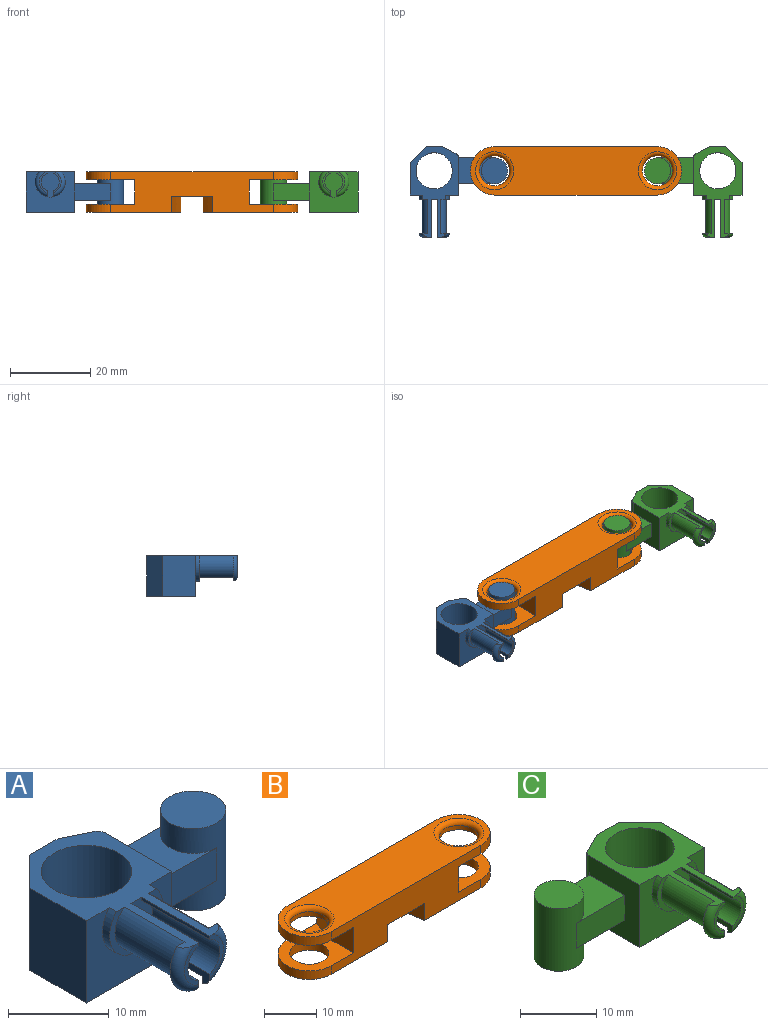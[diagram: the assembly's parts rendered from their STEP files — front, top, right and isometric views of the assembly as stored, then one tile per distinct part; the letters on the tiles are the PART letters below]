
ASSEMBLY  parts=3 mates=2
PART A: 33 faces, bbox 24.4x22.6x11.3 mm
  f0: plane 6.17x3mm, normal (0,1,0), area 5.5mm2, adj f3,f4,f27,f31
  f1: plane 9.5x0.38mm, normal (-1,0,0), area 3.6mm2, adj f2,f4,f5,f6
  f2: cylinder r=2.25mm len=9.5mm, axis (0,1,0), area 52.6mm2, adj f1,f3,f5,f6
  f3: plane 9.64x1.69mm, normal (-1,0,0), area 8mm2, adj f0,f2,f5,f6,f27,f31
  f4: plane 22.5x12mm, normal (0,0,1), area 92.8mm2, adj f0,f1,f5,f6,f7,f8,f10,f11
  f5: plane 5.15x2mm, normal (0,-1,0), area 3.1mm2, adj f1,f2,f3,f4,f31
  f6: plane 7.5x6.25mm, normal (0,-1,0), area 29.7mm2, adj f1,f2,f3,f4,f18,f21,f24,f25
  f7: plane 10x8mm, normal (-1,0,0), area 80mm2, adj f4,f9,f10,f19
  f8: plane 10x9.38mm, normal (1,0,0), area 67.8mm2, adj f4,f9,f14,f15,f16,f17,f19,f20
  f9: plane 12x12mm, normal (0,0,-1), area 68.3mm2, adj f7,f8,f10,f11,f12,f13,f19,f20
  f10: plane 10x4mm, normal (-0.71,0.71,0), area 56.6mm2, adj f4,f7,f9,f13
  f11: plane 10x3.45mm, normal (0.45,0.89,0), area 38.5mm2, adj f4,f9,f13,f20
  f12: cylinder r=4.5mm len=10mm, axis (0,0,-1), area 282.7mm2, adj f4,f9
  f13: plane 10x4mm, normal (0,1,0), area 40mm2, adj f4,f9,f10,f11
  f14: plane 9x4mm, normal (0,1,0), area 36mm2, adj f8,f16,f17,f28
  f15: plane 9x4mm, normal (0,-1,0), area 36mm2, adj f8,f16,f17,f28
  f16: plane 9x6.5mm, normal (0,0,1), area 41.9mm2, adj f8,f14,f15,f28
  f17: plane 9x6.5mm, normal (0,0,-1), area 41.9mm2, adj f8,f14,f15,f28
  f18: cylinder r=3.75mm len=7.5mm, axis (0,-1,0), area 17.3mm2, adj f4,f6,f19
  f19: plane 12x10mm, normal (0,-1,0), area 80.7mm2, adj f4,f7,f8,f9,f18
  f20: cylinder r=1mm len=10mm, axis (0,0,-1), area 11.1mm2, adj f4,f8,f9,f11
  f21: plane 9.64x1.69mm, normal (1,0,0), area 8mm2, adj f6,f22,f23,f24,f26,f32
  f22: plane 5.15x2mm, normal (0,-1,0), area 3.1mm2, adj f4,f21,f24,f25,f32
  f23: plane 6.17x3mm, normal (0,1,0), area 5.5mm2, adj f4,f21,f26,f32
  f24: cylinder r=2.25mm len=9.5mm, axis (0,1,0), area 52.6mm2, adj f6,f21,f22,f25
  f25: plane 9.5x0.38mm, normal (1,0,0), area 3.6mm2, adj f4,f6,f22,f24
  f26: cylinder r=3mm len=8.5mm, axis (0,1,0), area 58.7mm2, adj f4,f6,f21,f23
  f27: cylinder r=3mm len=8.5mm, axis (0,1,0), area 58.7mm2, adj f0,f3,f4,f6
  f28: cylinder r=3.25mm len=10mm, axis (0,0,-1), area 163.4mm2, adj f14,f15,f16,f17,f29,f30
  f29: plane 6.5x6.5mm, normal (0,0,1), area 33.2mm2, adj f28
  f30: plane 6.5x6.5mm, normal (0,0,-1), area 33.2mm2, adj f28
  f31: torus R=2.75mm, axis (0,-1,0), area 11.6mm2, adj f0,f3,f4,f5
  f32: torus R=2.75mm, axis (0,-1,0), area 11.6mm2, adj f4,f21,f22,f23
PART B: 26 faces, bbox 52.5x12.4x10 mm
  f0: plane 40.5x10mm, normal (0,1,0), area 286.5mm2, adj f1,f2,f5,f6,f7,f11,f12,f13
  f1: plane 23.83x12.39mm, normal (0,0,-1), area 207.6mm2, adj f0,f7,f8,f9,f21
  f2: cylinder r=6mm len=12mm, axis (0,0,-1), area 37.7mm2, adj f0,f8,f11,f16
  f3: cylinder r=3.75mm len=7.5mm, axis (0,0,-1), area 23.6mm2, adj f16,f25
  f4: cylinder r=3.75mm len=7.5mm, axis (0,0,-1), area 23.6mm2, adj f13,f24
  f5: cylinder r=6mm len=12mm, axis (0,0,-1), area 37.7mm2, adj f0,f8,f11,f13
  f6: cylinder r=6mm len=12mm, axis (0,0,-1), area 37.7mm2, adj f0,f8,f12,f14
  f7: cylinder r=6mm len=12mm, axis (0,0,-1), area 37.7mm2, adj f0,f1,f8,f17
  f8: plane 40.5x10mm, normal (0,-1,0), area 293mm2, adj f1,f2,f5,f6,f7,f11,f12,f13
  f9: cylinder r=3.75mm len=7.5mm, axis (0,0,-1), area 47.1mm2, adj f1,f17
  f10: cylinder r=3.75mm len=7.5mm, axis (0,0,-1), area 47.1mm2, adj f12,f14
  f11: plane 52.5x12mm, normal (0,0,1), area 457.3mm2, adj f0,f2,f5,f8,f24,f25
  f12: plane 23.83x12.39mm, normal (0,0,-1), area 207.6mm2, adj f0,f6,f8,f10,f22
  f13: plane 14x12mm, normal (0,0,-1), area 89.4mm2, adj f0,f4,f5,f8,f15,f19
  f14: plane 14x12mm, normal (0,0,1), area 89.4mm2, adj f0,f6,f8,f10,f15,f19
  f15: plane 7x6mm, normal (1,0,0), area 42mm2, adj f8,f13,f14,f19
  f16: plane 14x12mm, normal (0,0,-1), area 89.4mm2, adj f0,f2,f3,f8,f18,f20
  f17: plane 14x12mm, normal (0,0,1), area 89.4mm2, adj f0,f7,f8,f9,f18,f20
  f18: plane 7x6mm, normal (-1,0,0), area 42mm2, adj f8,f16,f17,f20
  f19: plane 6x5mm, normal (0.93,0.37,0), area 32.3mm2, adj f0,f13,f14,f15
  f20: plane 6x5mm, normal (-0.93,0.37,0), area 32.3mm2, adj f0,f16,f17,f18
  f21: extruded ~12x4mm, area 48.8mm2, adj f0,f1,f8,f23
  f22: extruded ~12x4mm, area 48.8mm2, adj f0,f8,f12,f23
  f23: plane 12.39x10mm, normal (0,0,-1), area 95.6mm2, adj f0,f8,f21,f22
  f24: torus R=4.75mm, axis (0,0,1), area 40.6mm2, adj f4,f11
  f25: torus R=4.75mm, axis (0,0,1), area 40.6mm2, adj f3,f11
PART C: 33 faces, bbox 24.4x22.6x11.3 mm
  f0: plane 6.17x3mm, normal (0,1,0), area 5.5mm2, adj f3,f4,f27,f31
  f1: plane 9.5x0.38mm, normal (1,0,0), area 3.6mm2, adj f2,f4,f5,f6
  f2: cylinder r=2.25mm len=9.5mm, axis (0,1,0), area 52.6mm2, adj f1,f3,f5,f6
  f3: plane 9.64x1.69mm, normal (1,0,0), area 8mm2, adj f0,f2,f5,f6,f27,f31
  f4: plane 22.5x12mm, normal (0,0,1), area 92.8mm2, adj f0,f1,f5,f6,f7,f8,f10,f11
  f5: plane 5.15x2mm, normal (0,-1,0), area 3.1mm2, adj f1,f2,f3,f4,f31
  f6: plane 7.5x6.25mm, normal (0,-1,0), area 29.7mm2, adj f1,f2,f3,f4,f18,f21,f24,f25
  f7: plane 10x8mm, normal (1,0,0), area 80mm2, adj f4,f9,f10,f19
  f8: plane 10x9.38mm, normal (-1,0,0), area 67.8mm2, adj f4,f9,f14,f15,f16,f17,f19,f20
  f9: plane 12x12mm, normal (0,0,-1), area 68.3mm2, adj f7,f8,f10,f11,f12,f13,f19,f20
  f10: plane 10x4mm, normal (0.71,0.71,0), area 56.6mm2, adj f4,f7,f9,f13
  f11: plane 10x3.45mm, normal (-0.45,0.89,0), area 38.5mm2, adj f4,f9,f13,f20
  f12: cylinder r=4.5mm len=10mm, axis (0,0,-1), area 282.7mm2, adj f4,f9
  f13: plane 10x4mm, normal (0,1,0), area 40mm2, adj f4,f9,f10,f11
  f14: plane 9x4mm, normal (0,1,0), area 36mm2, adj f8,f16,f17,f28
  f15: plane 9x4mm, normal (0,-1,0), area 36mm2, adj f8,f16,f17,f28
  f16: plane 9x6.5mm, normal (0,0,1), area 41.9mm2, adj f8,f14,f15,f28
  f17: plane 9x6.5mm, normal (0,0,-1), area 41.9mm2, adj f8,f14,f15,f28
  f18: cylinder r=3.75mm len=7.5mm, axis (0,-1,0), area 17.3mm2, adj f4,f6,f19
  f19: plane 12x10mm, normal (0,-1,0), area 80.7mm2, adj f4,f7,f8,f9,f18
  f20: cylinder r=1mm len=10mm, axis (0,0,-1), area 11.1mm2, adj f4,f8,f9,f11
  f21: plane 9.64x1.69mm, normal (-1,0,0), area 8mm2, adj f6,f22,f23,f24,f26,f32
  f22: plane 5.15x2mm, normal (0,-1,0), area 3.1mm2, adj f4,f21,f24,f25,f32
  f23: plane 6.17x3mm, normal (0,1,0), area 5.5mm2, adj f4,f21,f26,f32
  f24: cylinder r=2.25mm len=9.5mm, axis (0,1,0), area 52.6mm2, adj f6,f21,f22,f25
  f25: plane 9.5x0.38mm, normal (-1,0,0), area 3.6mm2, adj f4,f6,f22,f24
  f26: cylinder r=3mm len=8.5mm, axis (0,1,0), area 58.7mm2, adj f4,f6,f21,f23
  f27: cylinder r=3mm len=8.5mm, axis (0,1,0), area 58.7mm2, adj f0,f3,f4,f6
  f28: cylinder r=3.25mm len=10mm, axis (0,0,-1), area 163.4mm2, adj f14,f15,f16,f17,f29,f30
  f29: plane 6.5x6.5mm, normal (0,0,1), area 33.2mm2, adj f28
  f30: plane 6.5x6.5mm, normal (0,0,-1), area 33.2mm2, adj f28
  f31: torus R=2.75mm, axis (0,-1,0), area 11.6mm2, adj f0,f3,f4,f5
  f32: torus R=2.75mm, axis (0,-1,0), area 11.6mm2, adj f4,f21,f22,f23
PLACE A t=(-34.56,41.7,102.95)mm
PLACE B t=(50.64,73.96,102.95)mm
PLACE C t=(77.99,41.7,102.95)mm
MATE fastened C.f28 <-> B.f4  axis (0,0,1) through (41.96,31.19,112.95)mm
MATE fastened A.f28 <-> B.f2  axis (0,0,1) through (1.46,31.19,112.95)mm
